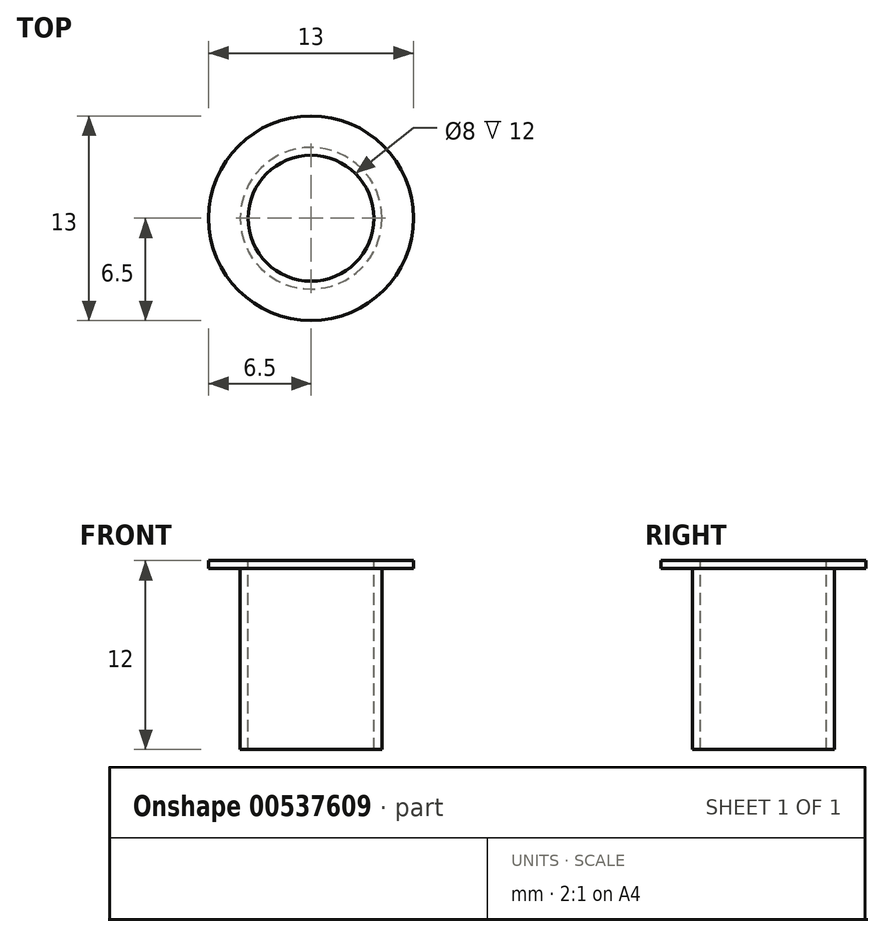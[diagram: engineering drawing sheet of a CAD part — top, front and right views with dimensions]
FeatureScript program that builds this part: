
annotation { "Feature Type Name" : "Feature", "Feature Type Description" : "" }
export const myFeature = defineFeature(function(context is Context, id is Id, definition is map)
    precondition{}
    {
        {
            var Q0;
            Q0=qCreatedBy(makeId("Right.planeOp"),FACE);
            var sketch = newSketch(context, id + "F0", { "sketchPlane" : qUnion([Q0])});
            skLineSegment(sketch, "E0", {"start": v(4, 12) * mm, "end": v(6.5, 12) * mm});
            skLineSegment(sketch, "E1", {"start": v(6.5, 12) * mm, "end": v(6.5, 11.5) * mm});
            skLineSegment(sketch, "E2", {"start": v(6.5, 11.5) * mm, "end": v(4.5, 11.5) * mm});
            skLineSegment(sketch, "E3", {"start": v(4.5, 11.5) * mm, "end": v(4.5, 0) * mm});
            skLineSegment(sketch, "E4", {"start": v(4.5, 0) * mm, "end": v(4, 0) * mm});
            skLineSegment(sketch, "E5", {"start": v(4, 0) * mm, "end": v(4, 12) * mm});
            skLineSegment(sketch, "E6", {"start": v(0, 15.48) * mm, "end": v(0, 0) * mm});
            skSolve(sketch);
        }
        {
            var Q0;
            Q0=makeQuery(id+"F0.imprint","IMPRINT",FACE,{"disambiguationData":[TD([[makeQuery(id+"F0.imprint","IMPRINT",EDGE,{"derivedFrom":sQuery(id+"F0.wireOp",EDGE,"E0")}),-1.0]])]});
            var Q1;
            Q1=sQuery(id+"F0.wireOp",EDGE,"E6");
            revolve(context, id + "F1", {"entities" : qUnion([Q0]), "axis" : qUnion([Q1]), "revolveType" : RevolveType.FULL});
        }
    });
